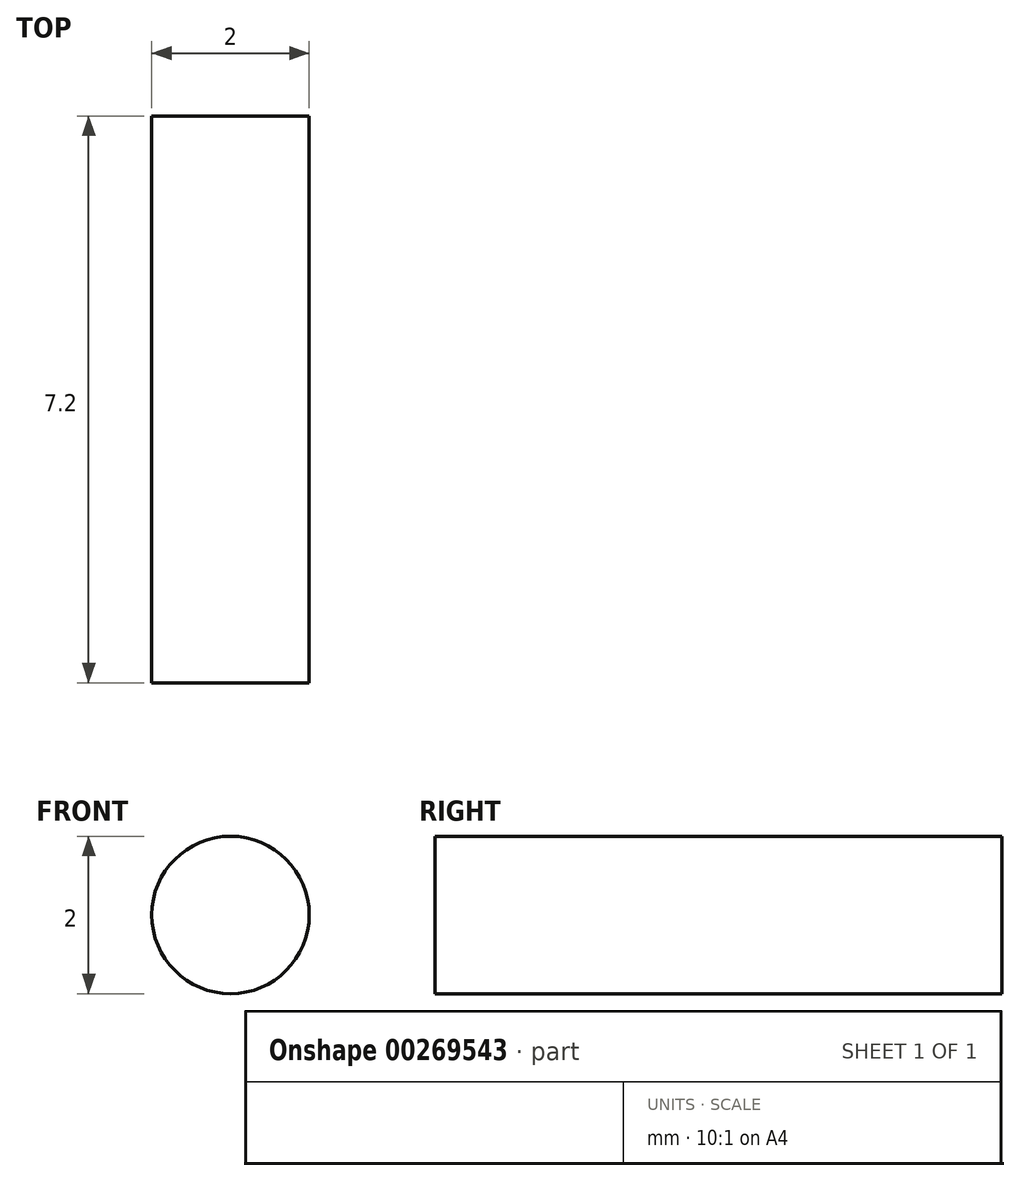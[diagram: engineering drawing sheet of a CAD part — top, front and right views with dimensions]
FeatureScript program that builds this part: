
annotation { "Feature Type Name" : "Feature", "Feature Type Description" : "" }
export const myFeature = defineFeature(function(context is Context, id is Id, definition is map)
    precondition{}
    {
        {
            var Q0;
            Q0=qCreatedBy(makeId("Front.planeOp"),FACE);
            var sketch = newSketch(context, id + "F0", { "sketchPlane" : qUnion([Q0])});
            skCircle(sketch, "E0", {"center": v(0, 0) * mm, "radius": 1 * mm});
            skSolve(sketch);
        }
        {
            var Q0;
            Q0=makeQuery(id+"F0.imprint","IMPRINT",FACE,{"disambiguationData":[TD([[makeQuery(id+"F0.imprint","IMPRINT",EDGE,{"derivedFrom":sQuery(id+"F0.wireOp",EDGE,"E0")}),1.0]])]});
            extrude(context, id + "F1", {"entities" : qUnion([Q0]), "endBound" : BoundingType.SYMMETRIC, "depth" : 7.2 * mm});
        }
    });
